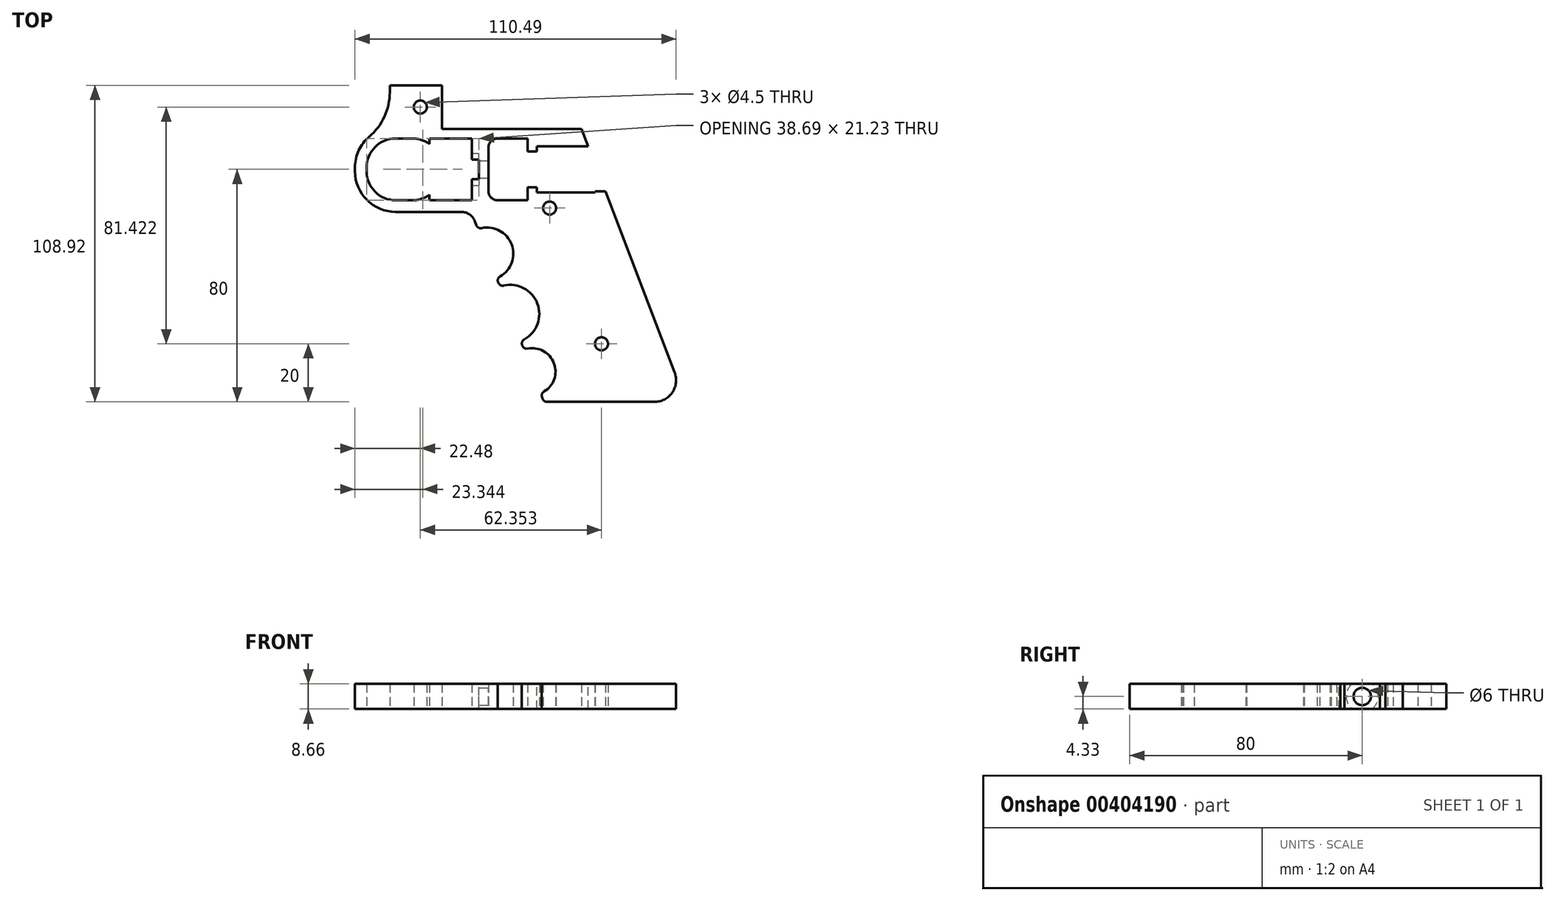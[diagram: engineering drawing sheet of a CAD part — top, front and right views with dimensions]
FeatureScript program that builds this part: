
annotation { "Feature Type Name" : "Feature", "Feature Type Description" : "" }
export const myFeature = defineFeature(function(context is Context, id is Id, definition is map)
    precondition{}
    {
        {
            var Q0;
            Q0=qCreatedBy(makeId("Top.planeOp"),FACE);
            var sketch = newSketch(context, id + "F0", { "sketchPlane" : qUnion([Q0])});
            skLineSegment(sketch, "E0", {"start": v(0, 27.49) * mm, "end": v(20, -24.82) * mm});
            skLineSegment(sketch, "E1", {"start": v(13, -35) * mm, "end": v(-25, -35) * mm});
            skLineSegment(sketch, "E2", {"start": v(-25, -35) * mm, "end": v(-26.14, -32.01) * mm});
            skLineSegment(sketch, "E3", {"start": v(-50, 30.38) * mm, "end": v(-76, 30.38) * mm});
            skLineSegment(sketch, "E4", {"start": v(-90, 44.38) * mm, "end": v(-90, 60.38) * mm});
            skLineSegment(sketch, "E5.bottom", {"start": v(-76, 55.62) * mm, "end": v(-70.17, 55.62) * mm});
            skLineSegment(sketch, "E5.top", {"start": v(-76, 34.38) * mm, "end": v(-70.17, 34.38) * mm});
            skLineSegment(sketch, "E5.left", {"start": v(-86, 45.62) * mm, "end": v(-86, 44.38) * mm});
            skLineSegment(sketch, "E5.right", {"start": v(-53.96, 45.62) * mm, "end": v(-53.96, 44.38) * mm, "construction": true});
            skPoint(sketch, "E6.visualSharp", {"position": v(-86, 55.62) * mm});
            skArc(sketch, "E6.filletArc", {"start": v(-76, 55.62) * mm, "mid": v(-83.07, 52.69) * mm, "end": v(-86, 45.62) * mm});
            skPoint(sketch, "E7.visualSharp", {"position": v(-86, 34.38) * mm});
            skArc(sketch, "E7.filletArc", {"start": v(-86, 44.38) * mm, "mid": v(-83.07, 37.31) * mm, "end": v(-76, 34.38) * mm});
            skPoint(sketch, "E8.visualSharp", {"position": v(-53.96, 34.38) * mm});
            skPoint(sketch, "E9.visualSharp", {"position": v(-53.96, 55.62) * mm});
            skPoint(sketch, "E10.visualSharp", {"position": v(-90, 30.38) * mm});
            skArc(sketch, "E10.filletArc", {"start": v(-90, 44.38) * mm, "mid": v(-85.9, 34.48) * mm, "end": v(-76, 30.38) * mm});
            skArc(sketch, "E11", {"start": v(-26.14, -32.01) * mm, "mid": v(-21.53, -21.68) * mm, "end": v(-31.86, -17.07) * mm});
            skArc(sketch, "E12", {"start": v(-33, -14.08) * mm, "mid": v(-27.23, -1.17) * mm, "end": v(-40.14, 4.6) * mm});
            skArc(sketch, "E13", {"start": v(-41.29, 7.6) * mm, "mid": v(-36.1, 19.21) * mm, "end": v(-47.71, 24.4) * mm});
            skLineSegment(sketch, "E14.trimOffspring", {"start": v(-47.71, 24.4) * mm, "end": v(-50, 30.38) * mm});
            skLineSegment(sketch, "E15.trimOffspring", {"start": v(-40.14, 4.6) * mm, "end": v(-41.29, 7.6) * mm});
            skLineSegment(sketch, "E16.trimOffspring", {"start": v(-31.86, -17.07) * mm, "end": v(-33, -14.08) * mm});
            skCircle(sketch, "E17", {"center": v(-5.17, -15) * mm, "radius": 2.25 * mm});
            skCircle(sketch, "E18", {"center": v(-23.02, 31.7) * mm, "radius": 2.25 * mm});
            skLineSegment(sketch, "E19", {"start": v(-78.02, 73.92) * mm, "end": v(-60.02, 73.92) * mm});
            skLineSegment(sketch, "E20", {"start": v(-30.61, 51.12) * mm, "end": v(-25.61, 51.12) * mm});
            skLineSegment(sketch, "E21", {"start": v(-25.61, 51.12) * mm, "end": v(-25.61, 52.5) * mm});
            skLineSegment(sketch, "E22", {"start": v(-53.96, 45) * mm, "end": v(-22.83, 45) * mm, "construction": true});
            skLineSegment(sketch, "E23.MirrorCS", {"start": v(-30.61, 38.88) * mm, "end": v(-25.61, 38.88) * mm});
            skLineSegment(sketch, "E24.MirrorCS", {"start": v(-25.61, 38.88) * mm, "end": v(-25.61, 37.5) * mm});
            skLineSegment(sketch, "E25", {"start": v(-25.61, 52.5) * mm, "end": v(-12.61, 52.5) * mm});
            skLineSegment(sketch, "E26.MirrorCS", {"start": v(-25.61, 37.5) * mm, "end": v(-12.61, 37.5) * mm});
            skLineSegment(sketch, "E27", {"start": v(-12.61, 45) * mm, "end": v(-12.61, 45) * mm});
            skPoint(sketch, "E28.end.orphan", {"position": v(-15.65, 52.5) * mm});
            skPoint(sketch, "E28.start.orphan", {"position": v(-15.65, 45.74) * mm});
            skPoint(sketch, "E29.start.orphan", {"position": v(-15.65, 43.26) * mm});
            skPoint(sketch, "E30.orphan", {"position": v(-15.65, 37.5) * mm});
            skLineSegment(sketch, "E31", {"start": v(-30.61, 51.12) * mm, "end": v(-30.61, 51.12) * mm});
            skLineSegment(sketch, "E32.MirrorCS", {"start": v(-30.61, 38.88) * mm, "end": v(-30.61, 38.88) * mm});
            skLineSegment(sketch, "E33", {"start": v(-64.33, 55.62) * mm, "end": v(-47.31, 55.62) * mm});
            skLineSegment(sketch, "E34", {"start": v(-30.61, 55.62) * mm, "end": v(-30.61, 51.12) * mm});
            skLineSegment(sketch, "E35.MirrorCS", {"start": v(-64.33, 34.38) * mm, "end": v(-47.31, 34.38) * mm});
            skLineSegment(sketch, "E36.MirrorCS", {"start": v(-30.61, 34.38) * mm, "end": v(-30.61, 38.88) * mm});
            skPoint(sketch, "E37.orphan", {"position": v(-55.65, 38.88) * mm});
            skPoint(sketch, "E38.orphan", {"position": v(-55.65, 51.12) * mm});
            skCircle(sketch, "E39", {"center": v(-67.52, 66.42) * mm, "radius": 2.25 * mm});
            skArc(sketch, "E40", {"start": v(13, -35) * mm, "mid": v(19.17, -31.75) * mm, "end": v(20, -24.82) * mm});
            skPoint(sketch, "E41.orphan", {"position": v(23.9, -35) * mm});
            skLineSegment(sketch, "E42", {"start": v(0, 27.49) * mm, "end": v(-3.83, 37.5) * mm});
            skLineSegment(sketch, "E43", {"start": v(-60.02, 73.92) * mm, "end": v(-60.02, 58.92) * mm});
            skLineSegment(sketch, "E44", {"start": v(-60.02, 58.92) * mm, "end": v(-12.02, 58.92) * mm});
            skPoint(sketch, "E45.start.orphan", {"position": v(-17.76, 73.92) * mm});
            skPoint(sketch, "E46.orphan", {"position": v(-31.02, 73.92) * mm});
            skArc(sketch, "E47", {"start": v(-90, 45.62) * mm, "mid": v(-88.7, 51.5) * mm, "end": v(-85.07, 56.28) * mm});
            skLineSegment(sketch, "E48", {"start": v(-78.02, 73.92) * mm, "end": v(-78.02, 71.52) * mm});
            skArc(sketch, "E49", {"start": v(-85.07, 56.28) * mm, "mid": v(-79.87, 63.13) * mm, "end": v(-78.02, 71.52) * mm});
            skLineSegment(sketch, "E50", {"start": v(-60.02, 58.92) * mm, "end": v(-82.49, 58.92) * mm, "construction": true});
            skLineSegment(sketch, "E51", {"start": v(-60.02, 73.92) * mm, "end": v(-17.76, 73.92) * mm, "construction": true});
            skLineSegment(sketch, "E52", {"start": v(-12.02, 58.92) * mm, "end": v(-12.02, 73.92) * mm, "construction": true});
            skLineSegment(sketch, "E53", {"start": v(-12.02, 73.92) * mm, "end": v(-17.76, 73.92) * mm, "construction": true});
            skCircle(sketch, "E54", {"center": v(-30.02, 66.42) * mm, "radius": 2.25 * mm, "construction": true});
            skCircle(sketch, "E55", {"center": v(-50.02, 66.42) * mm, "radius": 2.25 * mm, "construction": true});
            skArc(sketch, "E56", {"start": v(-64.33, 55.62) * mm, "mid": v(-57.26, 52.69) * mm, "end": v(-54.33, 45.62) * mm, "construction": true});
            skArc(sketch, "E57", {"start": v(-64.33, 34.38) * mm, "mid": v(-57.26, 37.31) * mm, "end": v(-54.33, 44.38) * mm, "construction": true});
            skLineSegment(sketch, "E58", {"start": v(-54.33, 45.62) * mm, "end": v(-54.33, 44.38) * mm, "construction": true});
            skLineSegment(sketch, "E59", {"start": v(-9.56, 52.5) * mm, "end": v(-12.61, 52.5) * mm});
            skLineSegment(sketch, "E60", {"start": v(-3.83, 37.5) * mm, "end": v(-12.61, 37.5) * mm});
            skLineSegment(sketch, "E61.trimOffspring", {"start": v(-9.56, 52.5) * mm, "end": v(-12.02, 58.92) * mm});
            skLineSegment(sketch, "E62", {"start": v(-43.61, 55.62) * mm, "end": v(-43.61, 34.38) * mm, "construction": true});
            skLineSegment(sketch, "E63", {"start": v(-44.11, 55.62) * mm, "end": v(-44.11, 48.2) * mm});
            skLineSegment(sketch, "E64", {"start": v(-44.11, 48.2) * mm, "end": v(-47.31, 48.2) * mm});
            skLineSegment(sketch, "E65", {"start": v(-47.31, 48.2) * mm, "end": v(-47.31, 55.62) * mm});
            skLineSegment(sketch, "E66.MirrorCS", {"start": v(-44.11, 41.8) * mm, "end": v(-47.31, 41.8) * mm});
            skLineSegment(sketch, "E67.MirrorCS", {"start": v(-44.11, 34.38) * mm, "end": v(-44.11, 41.8) * mm});
            skLineSegment(sketch, "E68.MirrorCS", {"start": v(-47.31, 41.8) * mm, "end": v(-47.31, 34.38) * mm});
            skLineSegment(sketch, "E69.trimOffspring", {"start": v(-44.11, 55.62) * mm, "end": v(-30.61, 55.62) * mm});
            skLineSegment(sketch, "E70.trimOffspring", {"start": v(-44.11, 34.38) * mm, "end": v(-30.61, 34.38) * mm});
            skArc(sketch, "E71", {"start": v(-70.17, 34.38) * mm, "mid": v(-67.1, 34.86) * mm, "end": v(-64.33, 36.26) * mm});
            skLineSegment(sketch, "E72", {"start": v(-64.33, 36.26) * mm, "end": v(-64.33, 34.38) * mm});
            skLineSegment(sketch, "E73.MirrorCS", {"start": v(-64.33, 53.74) * mm, "end": v(-64.33, 55.62) * mm});
            skArc(sketch, "E74.MirrorCS", {"start": v(-70.17, 55.62) * mm, "mid": v(-67.1, 55.14) * mm, "end": v(-64.33, 53.74) * mm});
            skSolve(sketch);
        }
        {
            var Q0;
            Q0=qSketchRegion(id+"F0",true);
            extrude(context, id + "F1", {"entities" : qUnion([Q0]), "endBound" : BoundingType.SYMMETRIC, "depth" : 8.66 * mm});
        }
        {
            var Q0;
            Q0=qCreatedBy(makeId("Top.planeOp"),FACE);
            var sketch = newSketch(context, id + "F2", { "sketchPlane" : qUnion([Q0])});
            skLineSegment(sketch, "E75.bottom", {"start": v(-27.41, 53) * mm, "end": v(-7.41, 53) * mm});
            skLineSegment(sketch, "E75.top", {"start": v(-27.41, 37) * mm, "end": v(-7.41, 37) * mm});
            skLineSegment(sketch, "E75.left", {"start": v(-27.41, 53) * mm, "end": v(-27.41, 37) * mm});
            skLineSegment(sketch, "E75.right", {"start": v(-7.41, 53) * mm, "end": v(-7.41, 37) * mm});
            skLineSegment(sketch, "E76", {"start": v(-47.41, 55.82) * mm, "end": v(-47.41, 34.64) * mm, "construction": true});
            skSolve(sketch);
        }
        {
            var Q0;
            Q0 = qSketchRegion(id + "F2", true);
            extrude(context, id + "F3", {"entities" : qUnion([Q0]), "operationType" : NewBodyOperationType.REMOVE, "endBound" : BoundingType.SYMMETRIC, "oppositeDirection" : true, "depth" : 25 * mm});
        }
        {
            var Q0;
            Q0=makeQuery(id+"F1.opExtrude","SWEPT_EDGE",EDGE,{"disambiguationData":[OSD([sQuery(id+"F0.wireOp",EDGE,"E63"),sQuery(id+"F0.wireOp",EDGE,"E69.trimOffspring")])]});
            var Q1;
            Q1=makeQuery(id+"F1.opExtrude","SWEPT_EDGE",EDGE,{"disambiguationData":[OSD([sQuery(id+"F0.wireOp",EDGE,"E67.MirrorCS"),sQuery(id+"F0.wireOp",EDGE,"E70.trimOffspring")])]});
            fillet(context, id + "F4", {"entities" : qUnion([Q0, Q1]), "radius" : 3.2 * mm, "tangentPropagation" : true, "allowEdgeOverflow" : false});
        }
        {
            var Q0;
            Q0=makeQuery(id+"F1.opExtrude","SWEPT_FACE",FACE,{"disambiguationData":[OSD([sQuery(id+"F0.wireOp",EDGE,"E63")])]});
            var sketch = newSketch(context, id + "F5", { "sketchPlane" : qUnion([Q0])});
            skCircle(sketch, "E77", {"center": v(45, 0) * mm, "radius": 3 * mm});
            skLineSegment(sketch, "E78.bottom", {"start": v(41.8, 4.33) * mm, "end": v(48.2, 4.33) * mm});
            skLineSegment(sketch, "E78.top", {"start": v(41.8, -4.33) * mm, "end": v(48.2, -4.33) * mm});
            skLineSegment(sketch, "E78.left", {"start": v(41.8, 4.33) * mm, "end": v(41.8, -4.33) * mm});
            skLineSegment(sketch, "E78.right", {"start": v(48.2, 4.33) * mm, "end": v(48.2, -4.33) * mm});
            skLineSegment(sketch, "E79", {"start": v(41.8, 0) * mm, "end": v(48.2, 0) * mm, "construction": true});
            skSolve(sketch);
        }
        {
            var Q0;
            Q0 = qSketchRegion(id + "F5", true);
            extrude(context, id + "F6", {"entities" : qUnion([Q0]), "operationType" : NewBodyOperationType.ADD, "oppositeDirection" : true, "depth" : 3.2 * mm});
        }
        {
            var Q0;
            Q0=makeQuery(id+"F6.boolean.opBoolean","MERGE",FACE,{"derivedFrom":[makeQuery(id+"F1.opExtrude","SWEPT_FACE",FACE,{"disambiguationData":[OSD([sQuery(id+"F0.wireOp",EDGE,"E65")])]}),makeQuery(id+"F1.opExtrude","SWEPT_FACE",FACE,{"disambiguationData":[OSD([sQuery(id+"F0.wireOp",EDGE,"E68.MirrorCS")])]}),makeQuery(id+"F6.opExtrude","CAP_FACE",FACE,{"disambiguationData":[OSD([sQuery(id+"F5.wireOp",EDGE,"E77"),sQuery(id+"F5.wireOp",EDGE,"E78.bottom"),sQuery(id+"F5.wireOp",EDGE,"E78.top"),sQuery(id+"F5.wireOp",EDGE,"E78.left"),sQuery(id+"F5.wireOp",EDGE,"E78.right")])],"isStart":false})]});
            var sketch = newSketch(context, id + "F7", { "sketchPlane" : qUnion([Q0])});
            skLineSegment(sketch, "E80.bottom", {"start": v(-55.62, 4.33) * mm, "end": v(-48.4, 4.33) * mm});
            skLineSegment(sketch, "E80.top", {"start": v(-55.62, -4.33) * mm, "end": v(-48.4, -4.33) * mm});
            skLineSegment(sketch, "E80.left", {"start": v(-55.62, 4.33) * mm, "end": v(-55.62, -4.33) * mm});
            skLineSegment(sketch, "E80.right", {"start": v(-34.38, 4.33) * mm, "end": v(-34.38, -4.33) * mm});
            skPoint(sketch, "E80.middle", {"position": v(-45, 0) * mm});
            skArc(sketch, "E81", {"start": v(-41.6, -4.33) * mm, "mid": v(-39.5, 0) * mm, "end": v(-41.6, 4.33) * mm});
            skLineSegment(sketch, "E82.trimOffspring", {"start": v(-41.6, -4.33) * mm, "end": v(-34.38, -4.33) * mm});
            skLineSegment(sketch, "E83.trimOffspring", {"start": v(-41.6, 4.33) * mm, "end": v(-34.38, 4.33) * mm});
            skArc(sketch, "E84.trimOffspring", {"start": v(-48.4, 4.33) * mm, "mid": v(-50.5, 0) * mm, "end": v(-48.4, -4.33) * mm});
            skSolve(sketch);
        }
        {
            var Q0;
            Q0 = qSketchRegion(id + "F7", true);
            extrude(context, id + "F8", {"entities" : qUnion([Q0]), "operationType" : NewBodyOperationType.ADD, "depth" : 2.5 * mm});
        }
        {
            var Q0;
            Q0=makeQuery(id+"F1.opExtrude","SWEPT_EDGE",EDGE,{"disambiguationData":[OSD([sQuery(id+"F0.wireOp",EDGE,"E1"),sQuery(id+"F0.wireOp",EDGE,"E2")])]});
            var Q1;
            Q1=makeQuery(id+"F1.opExtrude","SWEPT_EDGE",EDGE,{"disambiguationData":[OSD([sQuery(id+"F0.wireOp",EDGE,"E2"),sQuery(id+"F0.wireOp",EDGE,"E11")])]});
            var Q2;
            Q2=makeQuery(id+"F1.opExtrude","SWEPT_EDGE",EDGE,{"disambiguationData":[OSD([sQuery(id+"F0.wireOp",EDGE,"E11"),sQuery(id+"F0.wireOp",EDGE,"E16.trimOffspring")])]});
            var Q3;
            Q3=makeQuery(id+"F1.opExtrude","SWEPT_EDGE",EDGE,{"disambiguationData":[OSD([sQuery(id+"F0.wireOp",EDGE,"E12"),sQuery(id+"F0.wireOp",EDGE,"E16.trimOffspring")])]});
            var Q4;
            Q4=makeQuery(id+"F1.opExtrude","SWEPT_EDGE",EDGE,{"disambiguationData":[OSD([sQuery(id+"F0.wireOp",EDGE,"E12"),sQuery(id+"F0.wireOp",EDGE,"E15.trimOffspring")])]});
            var Q5;
            Q5=makeQuery(id+"F1.opExtrude","SWEPT_EDGE",EDGE,{"disambiguationData":[OSD([sQuery(id+"F0.wireOp",EDGE,"E13"),sQuery(id+"F0.wireOp",EDGE,"E15.trimOffspring")])]});
            var Q6;
            Q6=makeQuery(id+"F1.opExtrude","SWEPT_EDGE",EDGE,{"disambiguationData":[OSD([sQuery(id+"F0.wireOp",EDGE,"E13"),sQuery(id+"F0.wireOp",EDGE,"E14.trimOffspring")])]});
            fillet(context, id + "F9", {"entities" : qUnion([Q0, Q1, Q2, Q3, Q4, Q5, Q6]), "radius" : 1.6 * mm, "tangentPropagation" : true, "allowEdgeOverflow" : false});
        }
        {
            var Q0;
            Q0=makeQuery(id+"F1.opExtrude","SWEPT_EDGE",EDGE,{"disambiguationData":[OSD([sQuery(id+"F0.wireOp",EDGE,"E3"),sQuery(id+"F0.wireOp",EDGE,"E14.trimOffspring")])]});
            fillet(context, id + "F10", {"entities" : qUnion([Q0]), "radius" : 5 * mm, "tangentPropagation" : true, "allowEdgeOverflow" : false});
        }
    });
